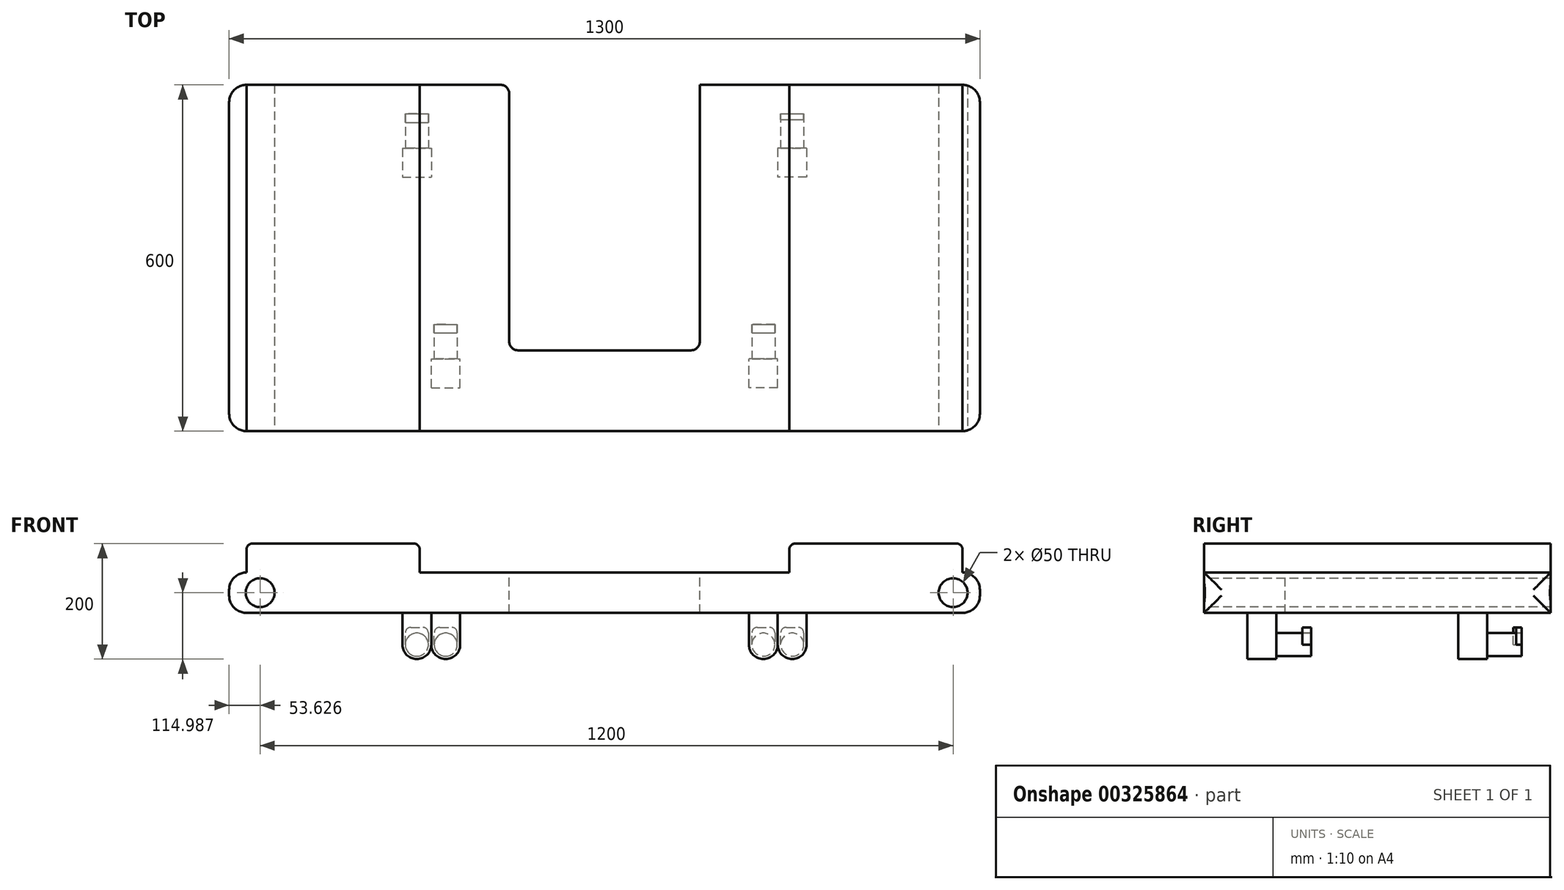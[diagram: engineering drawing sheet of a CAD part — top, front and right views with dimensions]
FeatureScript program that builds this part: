
annotation { "Feature Type Name" : "Feature", "Feature Type Description" : "" }
export const myFeature = defineFeature(function(context is Context, id is Id, definition is map)
    precondition{}
    {
        {
            var Q0;
            Q0=qCreatedBy(makeId("Front.planeOp"),FACE);
            var sketch = newSketch(context, id + "F0", { "sketchPlane" : qUnion([Q0])});
            skLineSegment(sketch, "E0.bottom", {"start": v(0, 0) * mm, "end": v(1300, 0) * mm});
            skLineSegment(sketch, "E0.top", {"start": v(0, 70) * mm, "end": v(1300, 70) * mm});
            skLineSegment(sketch, "E0.left", {"start": v(0, 0) * mm, "end": v(0, 70) * mm});
            skLineSegment(sketch, "E0.right", {"start": v(1300, 0) * mm, "end": v(1300, 70) * mm});
            skSolve(sketch);
        }
        {
            var Q0;
            Q0=makeQuery(id+"F0.imprint","IMPRINT",FACE,{"disambiguationData":[TD([[makeQuery(id+"F0.imprint","IMPRINT",EDGE,{"derivedFrom":sQuery(id+"F0.wireOp",EDGE,"E0.bottom")}),1.0]])]});
            extrude(context, id + "F1", {"entities" : qUnion([Q0]), "depth" : 600 * mm});
        }
        {
            var Q0;
            Q0=makeQuery(id+"F1.opExtrude","CAP_FACE",FACE,{"disambiguationData":[OSD([sQuery(id+"F0.wireOp",EDGE,"E0.bottom"),sQuery(id+"F0.wireOp",EDGE,"E0.top"),sQuery(id+"F0.wireOp",EDGE,"E0.left"),sQuery(id+"F0.wireOp",EDGE,"E0.right")])],"isStart":false});
            var sketch = newSketch(context, id + "F2", { "sketchPlane" : qUnion([Q0])});
            skCircle(sketch, "E1", {"center": v(53.63, 34.99) * mm, "radius": 25 * mm});
            skCircle(sketch, "E2", {"center": v(1253.63, 34.99) * mm, "radius": 25 * mm});
            skSolve(sketch);
        }
        {
            var Q0;
            Q0=makeQuery(id+"F2.imprint","IMPRINT",FACE,{"disambiguationData":[TD([[makeQuery(id+"F2.imprint","IMPRINT",EDGE,{"derivedFrom":sQuery(id+"F2.wireOp",EDGE,"E1")}),1.0]])]});
            var Q1;
            Q1=makeQuery(id+"F2.imprint","IMPRINT",FACE,{"disambiguationData":[TD([[makeQuery(id+"F2.imprint","IMPRINT",EDGE,{"derivedFrom":sQuery(id+"F2.wireOp",EDGE,"E2")}),1.0]])]});
            extrude(context, id + "F3", {"entities" : qUnion([Q0, Q1]), "operationType" : NewBodyOperationType.REMOVE, "oppositeDirection" : true, "depth" : 800 * mm});
        }
        {
            var Q0;
            Q0=makeQuery(id+"F1.opExtrude","SWEPT_FACE",FACE,{"disambiguationData":[OSD([sQuery(id+"F0.wireOp",EDGE,"E0.left")])]});
            var Q1;
            Q1=makeQuery(id+"F1.opExtrude","SWEPT_FACE",FACE,{"disambiguationData":[OSD([sQuery(id+"F0.wireOp",EDGE,"E0.right")])]});
            fillet(context, id + "F4", {"entities" : qUnion([Q0, Q1]), "radius" : 30 * mm, "tangentPropagation" : true, "allowEdgeOverflow" : false});
        }
        {
            var Q0;
            Q0=makeQuery(id+"F1.opExtrude","SWEPT_FACE",FACE,{"disambiguationData":[OSD([sQuery(id+"F0.wireOp",EDGE,"E0.top")])]});
            var sketch = newSketch(context, id + "F5", { "sketchPlane" : qUnion([Q0])});
            skLineSegment(sketch, "E3.bottom", {"start": v(485, 0) * mm, "end": v(815, 0) * mm});
            skLineSegment(sketch, "E3.top", {"start": v(485, -460) * mm, "end": v(815, -460) * mm});
            skLineSegment(sketch, "E3.left", {"start": v(485, 0) * mm, "end": v(485, -460) * mm});
            skLineSegment(sketch, "E3.right", {"start": v(815, 0) * mm, "end": v(815, -460) * mm});
            skSolve(sketch);
        }
        {
            var Q0;
            Q0=makeQuery(id+"F5.imprint","IMPRINT",FACE,{"disambiguationData":[TD([[makeQuery(id+"F5.imprint","IMPRINT",EDGE,{"derivedFrom":sQuery(id+"F5.wireOp",EDGE,"E3.bottom")}),-1.0]])]});
            extrude(context, id + "F6", {"entities" : qUnion([Q0]), "operationType" : NewBodyOperationType.REMOVE, "oppositeDirection" : true, "depth" : 100 * mm});
        }
        {
            var Q0;
            Q0=makeQuery(id+"F6.boolean.opBoolean","COPY",EDGE,{"derivedFrom":makeQuery(id+"F6.opExtrude","SWEPT_EDGE",EDGE,{"disambiguationData":[OSD([sQuery(id+"F0.wireOp",EDGE,"E0.top"),sQuery(id+"F5.wireOp",EDGE,"E3.bottom"),sQuery(id+"F5.wireOp",EDGE,"E3.right")])]})});
            var Q1;
            Q1=makeQuery(id+"F6.boolean.opBoolean","COPY",EDGE,{"derivedFrom":makeQuery(id+"F6.opExtrude","SWEPT_EDGE",EDGE,{"disambiguationData":[OSD([sQuery(id+"F0.wireOp",EDGE,"E0.top"),sQuery(id+"F5.wireOp",EDGE,"E3.bottom"),sQuery(id+"F5.wireOp",EDGE,"E3.left")])]})});
            var Q2;
            Q2=makeQuery(id+"F6.boolean.opBoolean","COPY",EDGE,{"derivedFrom":makeQuery(id+"F6.opExtrude","SWEPT_EDGE",EDGE,{"disambiguationData":[OSD([sQuery(id+"F5.wireOp",EDGE,"E3.top"),sQuery(id+"F5.wireOp",EDGE,"E3.left")])]})});
            var Q3;
            Q3=makeQuery(id+"F6.boolean.opBoolean","COPY",EDGE,{"derivedFrom":makeQuery(id+"F6.opExtrude","SWEPT_EDGE",EDGE,{"disambiguationData":[OSD([sQuery(id+"F5.wireOp",EDGE,"E3.top"),sQuery(id+"F5.wireOp",EDGE,"E3.right")])]})});
            fillet(context, id + "F7", {"entities" : qUnion([Q0, Q1, Q2, Q3]), "radius" : 15 * mm, "tangentPropagation" : true, "allowEdgeOverflow" : false});
        }
        {
            var Q0;
            Q0=makeQuery(id+"F1.opExtrude","SWEPT_FACE",FACE,{"disambiguationData":[OSD([sQuery(id+"F0.wireOp",EDGE,"E0.bottom")])]});
            var sketch = newSketch(context, id + "F8", { "sketchPlane" : qUnion([Q0])});
            skLineSegment(sketch, "E4.bottom", {"start": v(350, 525) * mm, "end": v(400, 525) * mm});
            skLineSegment(sketch, "E4.top", {"start": v(350, 475) * mm, "end": v(400, 475) * mm});
            skLineSegment(sketch, "E4.left", {"start": v(350, 525) * mm, "end": v(350, 475) * mm});
            skLineSegment(sketch, "E4.right", {"start": v(400, 525) * mm, "end": v(400, 475) * mm});
            skPoint(sketch, "E5.endSnap0", {"position": v(650, 600) * mm});
            skLineSegment(sketch, "E6.MirrorCS", {"start": v(950, 475) * mm, "end": v(900, 475) * mm});
            skLineSegment(sketch, "E7.MirrorCS", {"start": v(950, 525) * mm, "end": v(950, 475) * mm});
            skLineSegment(sketch, "E8.MirrorCS", {"start": v(950, 525) * mm, "end": v(900, 525) * mm});
            skLineSegment(sketch, "E9.MirrorCS", {"start": v(900, 525) * mm, "end": v(900, 475) * mm});
            skLineSegment(sketch, "E10.MirrorCS", {"start": v(950, 110) * mm, "end": v(950, 160) * mm});
            skLineSegment(sketch, "E11.MirrorCS", {"start": v(1000, 110) * mm, "end": v(950, 110) * mm});
            skLineSegment(sketch, "E12.MirrorCS", {"start": v(1000, 110) * mm, "end": v(1000, 160) * mm});
            skLineSegment(sketch, "E13.MirrorCS", {"start": v(300, 110) * mm, "end": v(300, 160) * mm});
            skLineSegment(sketch, "E14.MirrorCS", {"start": v(300, 160) * mm, "end": v(350, 160) * mm});
            skLineSegment(sketch, "E15.MirrorCS", {"start": v(300, 110) * mm, "end": v(350, 110) * mm});
            skLineSegment(sketch, "E16.MirrorCS", {"start": v(350, 110) * mm, "end": v(350, 160) * mm});
            skLineSegment(sketch, "E17.MirrorCS", {"start": v(1000, 160) * mm, "end": v(950, 160) * mm});
            skSolve(sketch);
        }
        {
            var Q0;
            Q0 = qSketchRegion(id + "F8", true);
            extrude(context, id + "F9", {"entities" : qUnion([Q0]), "operationType" : NewBodyOperationType.ADD, "depth" : 80 * mm});
        }
        {
            var Q0;
            Q0=makeQuery(id+"F9.opExtrude","CAP_EDGE",EDGE,{"disambiguationData":[OSD([sQuery(id+"F8.wireOp",EDGE,"E4.left")])],"isStart":false});
            var Q1;
            Q1=makeQuery(id+"F9.opExtrude","CAP_EDGE",EDGE,{"disambiguationData":[OSD([sQuery(id+"F8.wireOp",EDGE,"E4.right")])],"isStart":false});
            var Q2;
            Q2=makeQuery(id+"F9.opExtrude","CAP_EDGE",EDGE,{"disambiguationData":[OSD([sQuery(id+"F8.wireOp",EDGE,"E16.MirrorCS")])],"isStart":false});
            var Q3;
            Q3=makeQuery(id+"F9.opExtrude","CAP_EDGE",EDGE,{"disambiguationData":[OSD([sQuery(id+"F8.wireOp",EDGE,"E13.MirrorCS")])],"isStart":false});
            var Q4;
            Q4=makeQuery(id+"F9.opExtrude","CAP_EDGE",EDGE,{"disambiguationData":[OSD([sQuery(id+"F8.wireOp",EDGE,"E7.MirrorCS")])],"isStart":false});
            var Q5;
            Q5=makeQuery(id+"F9.opExtrude","CAP_EDGE",EDGE,{"disambiguationData":[OSD([sQuery(id+"F8.wireOp",EDGE,"E9.MirrorCS")])],"isStart":false});
            var Q6;
            Q6=makeQuery(id+"F9.opExtrude","CAP_EDGE",EDGE,{"disambiguationData":[OSD([sQuery(id+"F8.wireOp",EDGE,"E10.MirrorCS")])],"isStart":false});
            var Q7;
            Q7=makeQuery(id+"F9.opExtrude","CAP_EDGE",EDGE,{"disambiguationData":[OSD([sQuery(id+"F8.wireOp",EDGE,"E12.MirrorCS")])],"isStart":false});
            fillet(context, id + "F10", {"entities" : qUnion([Q0, Q1, Q2, Q3, Q4, Q5, Q6, Q7]), "radius" : 25 * mm, "tangentPropagation" : true, "allowEdgeOverflow" : false});
        }
        {
            var Q0;
            Q0=makeQuery(id+"F9.opExtrude","SWEPT_FACE",FACE,{"disambiguationData":[OSD([sQuery(id+"F8.wireOp",EDGE,"E11.MirrorCS")])]});
            var sketch = newSketch(context, id + "F11", { "sketchPlane" : qUnion([Q0])});
            skCircle(sketch, "E18", {"center": v(-975, -55) * mm, "radius": 20 * mm});
            skSolve(sketch);
        }
        {
            var Q0;
            Q0=makeQuery(id+"F11.imprint","IMPRINT",FACE,{"disambiguationData":[TD([[makeQuery(id+"F11.imprint","IMPRINT",EDGE,{"derivedFrom":sQuery(id+"F11.wireOp",EDGE,"E18")}),1.0]])]});
            extrude(context, id + "F12", {"entities" : qUnion([Q0]), "operationType" : NewBodyOperationType.ADD, "depth" : 60 * mm});
        }
        {
            var Q0;
            Q0=makeQuery(id+"F9.opExtrude","SWEPT_FACE",FACE,{"disambiguationData":[OSD([sQuery(id+"F8.wireOp",EDGE,"E15.MirrorCS")])]});
            var sketch = newSketch(context, id + "F13", { "sketchPlane" : qUnion([Q0])});
            skCircle(sketch, "E19", {"center": v(-325, -55) * mm, "radius": 20 * mm});
            skSolve(sketch);
        }
        {
            var Q0;
            Q0=makeQuery(id+"F13.imprint","IMPRINT",FACE,{"disambiguationData":[TD([[makeQuery(id+"F13.imprint","IMPRINT",EDGE,{"derivedFrom":sQuery(id+"F13.wireOp",EDGE,"E19")}),1.0]])]});
            extrude(context, id + "F14", {"entities" : qUnion([Q0]), "operationType" : NewBodyOperationType.ADD, "depth" : 60 * mm});
        }
        {
            var Q0;
            Q0=makeQuery(id+"F9.opExtrude","SWEPT_FACE",FACE,{"disambiguationData":[OSD([sQuery(id+"F8.wireOp",EDGE,"E4.top")])]});
            var sketch = newSketch(context, id + "F15", { "sketchPlane" : qUnion([Q0])});
            skCircle(sketch, "E20", {"center": v(-375, -55) * mm, "radius": 20 * mm});
            skSolve(sketch);
        }
        {
            var Q0;
            Q0=makeQuery(id+"F15.imprint","IMPRINT",FACE,{"disambiguationData":[TD([[makeQuery(id+"F15.imprint","IMPRINT",EDGE,{"derivedFrom":sQuery(id+"F15.wireOp",EDGE,"E20")}),1.0]])]});
            extrude(context, id + "F16", {"entities" : qUnion([Q0]), "operationType" : NewBodyOperationType.ADD, "depth" : 60 * mm});
        }
        {
            var Q0;
            Q0=makeQuery(id+"F9.opExtrude","SWEPT_FACE",FACE,{"disambiguationData":[OSD([sQuery(id+"F8.wireOp",EDGE,"E6.MirrorCS")])]});
            var sketch = newSketch(context, id + "F17", { "sketchPlane" : qUnion([Q0])});
            skCircle(sketch, "E21", {"center": v(-925, -55) * mm, "radius": 20 * mm});
            skSolve(sketch);
        }
        {
            var Q0;
            Q0=makeQuery(id+"F17.imprint","IMPRINT",FACE,{"disambiguationData":[TD([[makeQuery(id+"F17.imprint","IMPRINT",EDGE,{"derivedFrom":sQuery(id+"F17.wireOp",EDGE,"E21")}),1.0]])]});
            extrude(context, id + "F18", {"entities" : qUnion([Q0]), "operationType" : NewBodyOperationType.ADD, "depth" : 60 * mm});
        }
        {
            var Q0;
            Q0=makeQuery(id+"F1.opExtrude","SWEPT_FACE",FACE,{"disambiguationData":[OSD([sQuery(id+"F0.wireOp",EDGE,"E0.top")])]});
            var sketch = newSketch(context, id + "F19", { "sketchPlane" : qUnion([Q0])});
            skLineSegment(sketch, "E22.bottom", {"start": v(30, 0) * mm, "end": v(330, 0) * mm});
            skLineSegment(sketch, "E22.top", {"start": v(30, -600) * mm, "end": v(330, -600) * mm});
            skLineSegment(sketch, "E22.left", {"start": v(30, 0) * mm, "end": v(30, -600) * mm});
            skLineSegment(sketch, "E22.right", {"start": v(330, 0) * mm, "end": v(330, -600) * mm});
            skLineSegment(sketch, "E23.bottom", {"start": v(1270, -600) * mm, "end": v(970, -600) * mm});
            skLineSegment(sketch, "E23.top", {"start": v(1270, 0) * mm, "end": v(970, 0) * mm});
            skLineSegment(sketch, "E23.left", {"start": v(1270, -600) * mm, "end": v(1270, 0) * mm});
            skLineSegment(sketch, "E23.right", {"start": v(970, -600) * mm, "end": v(970, 0) * mm});
            skSolve(sketch);
        }
        {
            var Q0;
            Q0=makeQuery(id+"F19.imprint","IMPRINT",FACE,{"disambiguationData":[TD([[makeQuery(id+"F19.imprint","IMPRINT",EDGE,{"derivedFrom":sQuery(id+"F19.wireOp",EDGE,"E22.bottom")}),-1.0]])]});
            var Q1;
            Q1=makeQuery(id+"F19.imprint","IMPRINT",FACE,{"disambiguationData":[TD([[makeQuery(id+"F19.imprint","IMPRINT",EDGE,{"derivedFrom":sQuery(id+"F19.wireOp",EDGE,"E23.bottom")}),1.0]])]});
            extrude(context, id + "F20", {"entities" : qUnion([Q0, Q1]), "operationType" : NewBodyOperationType.ADD, "depth" : 50 * mm});
        }
        {
            var Q0;
            Q0=makeQuery(id+"F20.opExtrude","CAP_EDGE",EDGE,{"disambiguationData":[OSD([sQuery(id+"F19.wireOp",EDGE,"E23.left")])],"isStart":false});
            var Q1;
            Q1=makeQuery(id+"F20.opExtrude","CAP_EDGE",EDGE,{"disambiguationData":[OSD([sQuery(id+"F19.wireOp",EDGE,"E22.left")])],"isStart":false});
            var Q2;
            Q2=makeQuery(id+"F20.opExtrude","CAP_EDGE",EDGE,{"disambiguationData":[OSD([sQuery(id+"F19.wireOp",EDGE,"E22.right")])],"isStart":false});
            var Q3;
            Q3=makeQuery(id+"F20.opExtrude","CAP_EDGE",EDGE,{"disambiguationData":[OSD([sQuery(id+"F19.wireOp",EDGE,"E23.right")])],"isStart":false});
            fillet(context, id + "F21", {"entities" : qUnion([Q0, Q1, Q2, Q3]), "radius" : 10 * mm, "tangentPropagation" : true, "allowEdgeOverflow" : false});
        }
        {
            var Q0;
            Q0=makeQuery(id+"F12.opExtrude","CAP_FACE",FACE,{"disambiguationData":[OSD([sQuery(id+"F11.wireOp",EDGE,"E18")])],"isStart":false});
            var sketch = newSketch(context, id + "F22", { "sketchPlane" : qUnion([Q0])});
            skArc(sketch, "E24", {"start": v(-995, -55) * mm, "mid": v(-975, -75) * mm, "end": v(-955, -55) * mm});
            skLineSegment(sketch, "E25", {"start": v(-955, -55) * mm, "end": v(-955, -25) * mm});
            skLineSegment(sketch, "E26", {"start": v(-955, -25) * mm, "end": v(-995, -25) * mm});
            skLineSegment(sketch, "E27", {"start": v(-995, -25) * mm, "end": v(-995, -55) * mm});
            skSolve(sketch);
        }
        {
            var Q0;
            {var subQ0=sQuery(id+"F22.wireOp",EDGE,"E25");Q0=makeQuery(id+"F22.imprint","IMPRINT",FACE,{"disambiguationData":[TD([[makeQuery(id+"F22.imprint","IMPRINT",EDGE,{"derivedFrom":subQ0}),1.0]])]});}
            extrude(context, id + "F23", {"entities" : qUnion([Q0]), "oppositeDirection" : true, "depth" : 10 * mm});
        }
        {
            var Q0;
            Q0=makeQuery(id+"F18.opExtrude","CAP_FACE",FACE,{"disambiguationData":[OSD([sQuery(id+"F17.wireOp",EDGE,"E21")])],"isStart":false});
            var sketch = newSketch(context, id + "F24", { "sketchPlane" : qUnion([Q0])});
            skArc(sketch, "E28", {"start": v(-945, -55) * mm, "mid": v(-925, -75) * mm, "end": v(-905, -55) * mm});
            skLineSegment(sketch, "E29", {"start": v(-905, -55) * mm, "end": v(-905, -25) * mm});
            skLineSegment(sketch, "E30", {"start": v(-905, -25) * mm, "end": v(-945, -25) * mm});
            skLineSegment(sketch, "E31", {"start": v(-945, -25) * mm, "end": v(-945, -55) * mm});
            skSolve(sketch);
        }
        {
            var Q0;
            {var subQ0=sQuery(id+"F24.wireOp",EDGE,"E29");Q0=makeQuery(id+"F24.imprint","IMPRINT",FACE,{"disambiguationData":[TD([[makeQuery(id+"F24.imprint","IMPRINT",EDGE,{"derivedFrom":subQ0}),1.0]])]});}
            extrude(context, id + "F25", {"entities" : qUnion([Q0]), "oppositeDirection" : true, "depth" : 15 * mm});
        }
        {
            var Q0;
            Q0=makeQuery(id+"F23.opExtrude","SWEPT_EDGE",EDGE,{"disambiguationData":[OSD([sQuery(id+"F22.wireOp",EDGE,"E26"),sQuery(id+"F22.wireOp",EDGE,"E27")])]});
            var Q1;
            Q1=makeQuery(id+"F23.opExtrude","SWEPT_EDGE",EDGE,{"disambiguationData":[OSD([sQuery(id+"F22.wireOp",EDGE,"E25"),sQuery(id+"F22.wireOp",EDGE,"E26")])]});
            fillet(context, id + "F26", {"entities" : qUnion([Q0, Q1]), "radius" : 10 * mm, "tangentPropagation" : true, "allowEdgeOverflow" : false});
        }
        {
            var Q0;
            Q0=makeQuery(id+"F14.opExtrude","CAP_FACE",FACE,{"disambiguationData":[OSD([sQuery(id+"F13.wireOp",EDGE,"E19")])],"isStart":false});
            var sketch = newSketch(context, id + "F27", { "sketchPlane" : qUnion([Q0])});
            skArc(sketch, "E32", {"start": v(-345, -55) * mm, "mid": v(-325, -75) * mm, "end": v(-305, -55) * mm});
            skLineSegment(sketch, "E33", {"start": v(-305, -55) * mm, "end": v(-305, -25) * mm});
            skLineSegment(sketch, "E34", {"start": v(-305, -25) * mm, "end": v(-345, -25) * mm});
            skLineSegment(sketch, "E35", {"start": v(-345, -25) * mm, "end": v(-345, -55) * mm});
            skSolve(sketch);
        }
        {
            var Q0;
            {var subQ0=sQuery(id+"F27.wireOp",EDGE,"E33");Q0=makeQuery(id+"F27.imprint","IMPRINT",FACE,{"disambiguationData":[TD([[makeQuery(id+"F27.imprint","IMPRINT",EDGE,{"derivedFrom":subQ0}),1.0]])]});}
            extrude(context, id + "F28", {"entities" : qUnion([Q0]), "oppositeDirection" : true, "depth" : 15 * mm});
        }
        {
            var Q0;
            Q0=makeQuery(id+"F16.opExtrude","CAP_FACE",FACE,{"disambiguationData":[OSD([sQuery(id+"F15.wireOp",EDGE,"E20")])],"isStart":false});
            var sketch = newSketch(context, id + "F29", { "sketchPlane" : qUnion([Q0])});
            skArc(sketch, "E36", {"start": v(-395, -55) * mm, "mid": v(-375, -75) * mm, "end": v(-355, -55) * mm});
            skLineSegment(sketch, "E37", {"start": v(-355, -55) * mm, "end": v(-355, -25) * mm});
            skLineSegment(sketch, "E38", {"start": v(-355, -25) * mm, "end": v(-395, -25) * mm});
            skLineSegment(sketch, "E39", {"start": v(-395, -25) * mm, "end": v(-395, -55) * mm});
            skSolve(sketch);
        }
        {
            var Q0;
            {var subQ0=sQuery(id+"F29.wireOp",EDGE,"E37");Q0=makeQuery(id+"F29.imprint","IMPRINT",FACE,{"disambiguationData":[TD([[makeQuery(id+"F29.imprint","IMPRINT",EDGE,{"derivedFrom":subQ0}),1.0]])]});}
            extrude(context, id + "F30", {"entities" : qUnion([Q0]), "oppositeDirection" : true, "depth" : 15 * mm});
        }
        {
            var Q0;
            Q0=makeQuery(id+"F30.opExtrude","SWEPT_EDGE",EDGE,{"disambiguationData":[OSD([sQuery(id+"F29.wireOp",EDGE,"E38"),sQuery(id+"F29.wireOp",EDGE,"E39")])]});
            var Q1;
            Q1=makeQuery(id+"F28.opExtrude","SWEPT_EDGE",EDGE,{"disambiguationData":[OSD([sQuery(id+"F27.wireOp",EDGE,"E34"),sQuery(id+"F27.wireOp",EDGE,"E35")])]});
            var Q2;
            Q2=makeQuery(id+"F30.opExtrude","SWEPT_EDGE",EDGE,{"disambiguationData":[OSD([sQuery(id+"F29.wireOp",EDGE,"E37"),sQuery(id+"F29.wireOp",EDGE,"E38")])]});
            var Q3;
            Q3=makeQuery(id+"F28.opExtrude","SWEPT_EDGE",EDGE,{"disambiguationData":[OSD([sQuery(id+"F27.wireOp",EDGE,"E33"),sQuery(id+"F27.wireOp",EDGE,"E34")])]});
            var Q4;
            Q4=makeQuery(id+"F25.opExtrude","SWEPT_EDGE",EDGE,{"disambiguationData":[OSD([sQuery(id+"F24.wireOp",EDGE,"E29"),sQuery(id+"F24.wireOp",EDGE,"E30")])]});
            var Q5;
            Q5=makeQuery(id+"F25.opExtrude","SWEPT_EDGE",EDGE,{"disambiguationData":[OSD([sQuery(id+"F24.wireOp",EDGE,"E30"),sQuery(id+"F24.wireOp",EDGE,"E31")])]});
            fillet(context, id + "F31", {"entities" : qUnion([Q0, Q1, Q2, Q3, Q4, Q5]), "radius" : 10 * mm, "tangentPropagation" : true, "allowEdgeOverflow" : false});
        }
    });
